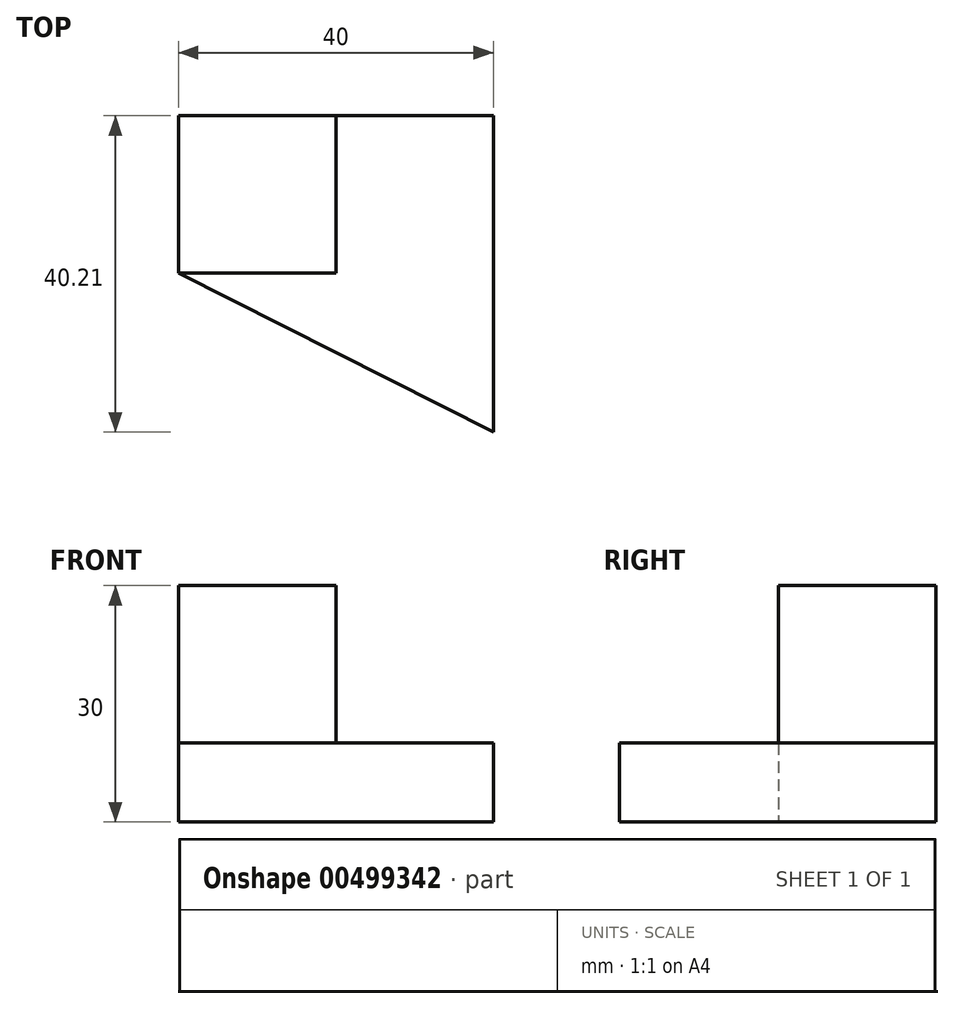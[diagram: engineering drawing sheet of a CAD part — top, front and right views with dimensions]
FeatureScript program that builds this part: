
annotation { "Feature Type Name" : "Feature", "Feature Type Description" : "" }
export const myFeature = defineFeature(function(context is Context, id is Id, definition is map)
    precondition{}
    {
        {
            var Q0;
            Q0=qCreatedBy(makeId("Top.planeOp"),FACE);
            var sketch = newSketch(context, id + "F0", { "sketchPlane" : qUnion([Q0])});
            skLineSegment(sketch, "E0", {"start": v(0, 0) * mm, "end": v(0, 20) * mm});
            skLineSegment(sketch, "E1", {"start": v(0, 20) * mm, "end": v(40, 20) * mm});
            skLineSegment(sketch, "E2", {"start": v(40, 20) * mm, "end": v(40, -20.21) * mm});
            skLineSegment(sketch, "E3", {"start": v(40, -20.21) * mm, "end": v(0, 0) * mm});
            skSolve(sketch);
        }
        {
            var Q0;
            Q0=makeQuery(id+"F0.imprint","IMPRINT",FACE,{"disambiguationData":[TD([[makeQuery(id+"F0.imprint","IMPRINT",EDGE,{"derivedFrom":sQuery(id+"F0.wireOp",EDGE,"E0")}),-1.0]])]});
            extrude(context, id + "F1", {"entities" : qUnion([Q0]), "depth" : 10 * mm});
        }
        {
            var Q0;
            Q0=makeQuery(id+"F1.opExtrude","CAP_FACE",FACE,{"disambiguationData":[OSD([sQuery(id+"F0.wireOp",EDGE,"E0"),sQuery(id+"F0.wireOp",EDGE,"E1"),sQuery(id+"F0.wireOp",EDGE,"E2"),sQuery(id+"F0.wireOp",EDGE,"E3")])],"isStart":false});
            var sketch = newSketch(context, id + "F2", { "sketchPlane" : qUnion([Q0])});
            skPoint(sketch, "E4.oppositeSnap0", {"position": v(20, -10.1) * mm});
            skLineSegment(sketch, "E4.bottom", {"start": v(0, 20) * mm, "end": v(20, 20) * mm});
            skLineSegment(sketch, "E4.top", {"start": v(0, 0) * mm, "end": v(20, 0) * mm});
            skLineSegment(sketch, "E4.left", {"start": v(0, 20) * mm, "end": v(0, 0) * mm});
            skLineSegment(sketch, "E4.right", {"start": v(20, 20) * mm, "end": v(20, 0) * mm});
            skSolve(sketch);
        }
        {
            var Q0;
            Q0=makeQuery(id+"F2.imprint","IMPRINT",FACE,{"disambiguationData":[TD([[makeQuery(id+"F2.imprint","IMPRINT",EDGE,{"derivedFrom":sQuery(id+"F2.wireOp",EDGE,"E4.bottom")}),-1.0]])]});
            extrude(context, id + "F3", {"entities" : qUnion([Q0]), "operationType" : NewBodyOperationType.ADD, "depth" : 20 * mm});
        }
    });
